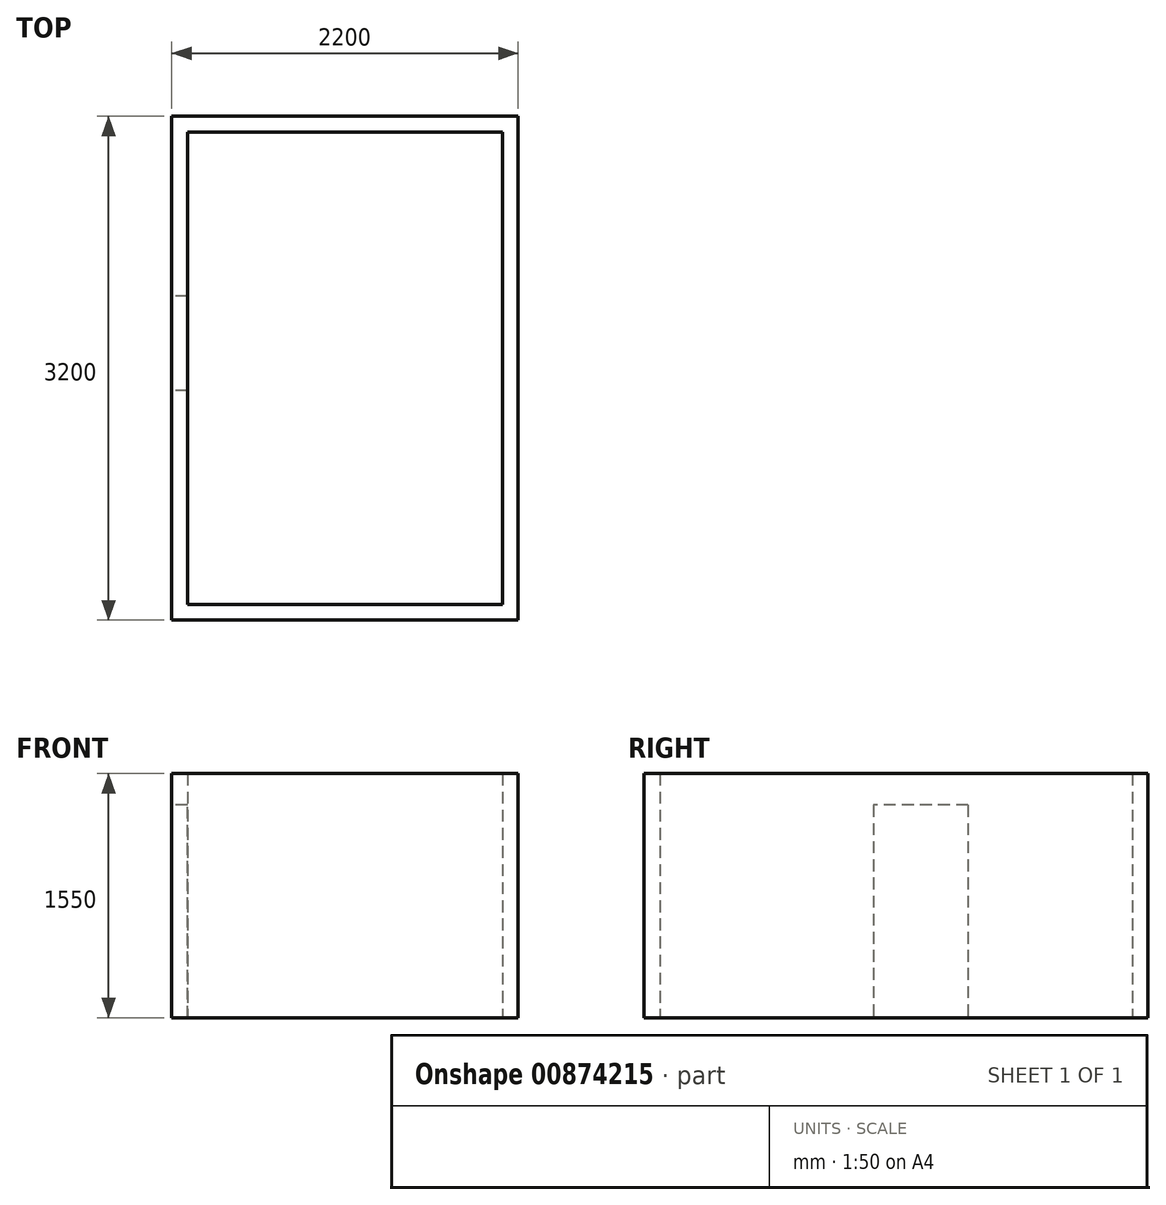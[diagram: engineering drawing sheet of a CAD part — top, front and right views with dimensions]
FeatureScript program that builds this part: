
annotation { "Feature Type Name" : "Feature", "Feature Type Description" : "" }
export const myFeature = defineFeature(function(context is Context, id is Id, definition is map)
    precondition{}
    {
        {
            var Q0;
            Q0=qCreatedBy(makeId("Top.planeOp"),FACE);
            var sketch = newSketch(context, id + "F0", { "sketchPlane" : qUnion([Q0])});
            skLineSegment(sketch, "E0", {"start": v(-780.9, 2929.22) * mm, "end": v(-780.9, -70.78) * mm});
            skLineSegment(sketch, "E1", {"start": v(-780.9, -70.78) * mm, "end": v(1219.1, -70.78) * mm});
            skLineSegment(sketch, "E2", {"start": v(1219.1, -70.78) * mm, "end": v(1219.1, 2929.22) * mm});
            skLineSegment(sketch, "E3", {"start": v(1219.1, 2929.22) * mm, "end": v(-780.9, 2929.22) * mm});
            skLineSegment(sketch, "E4", {"start": v(-780.9, 1429.22) * mm, "end": v(419.1, 1429.22) * mm});
            skLineSegment(sketch, "E5", {"start": v(419.1, 1429.22) * mm, "end": v(419.1, 2929.22) * mm});
            skArc(sketch, "E6", {"start": v(-480.9, 1429.22) * mm, "mid": v(-217.3, 2065.62) * mm, "end": v(419.1, 2329.22) * mm});
            skLineSegment(sketch, "E7.bottom", {"start": v(1219.1, 2929.22) * mm, "end": v(1319.1, 2929.22) * mm});
            skLineSegment(sketch, "E7.top", {"start": v(1219.1, -70.78) * mm, "end": v(1319.1, -70.78) * mm});
            skLineSegment(sketch, "E7.left", {"start": v(1219.1, 2929.22) * mm, "end": v(1219.1, -70.78) * mm});
            skLineSegment(sketch, "E7.right", {"start": v(1319.1, 2929.22) * mm, "end": v(1319.1, -70.78) * mm});
            skLineSegment(sketch, "E8.bottom", {"start": v(-780.9, 2929.22) * mm, "end": v(-880.9, 2929.22) * mm});
            skLineSegment(sketch, "E8.top", {"start": v(-780.9, -70.78) * mm, "end": v(-880.9, -70.78) * mm});
            skLineSegment(sketch, "E8.right", {"start": v(-880.9, 2929.22) * mm, "end": v(-880.9, -70.78) * mm});
            skLineSegment(sketch, "E9.bottom", {"start": v(-880.9, 2929.22) * mm, "end": v(1319.1, 2929.22) * mm});
            skLineSegment(sketch, "E9.top", {"start": v(-880.9, 3029.22) * mm, "end": v(1319.1, 3029.22) * mm});
            skLineSegment(sketch, "E9.left", {"start": v(-880.9, 2929.22) * mm, "end": v(-880.9, 3029.22) * mm});
            skLineSegment(sketch, "E9.right", {"start": v(1319.1, 2929.22) * mm, "end": v(1319.1, 3029.22) * mm});
            skLineSegment(sketch, "E10.bottom", {"start": v(-880.9, -70.78) * mm, "end": v(1319.1, -70.78) * mm});
            skLineSegment(sketch, "E10.top", {"start": v(-880.9, -170.78) * mm, "end": v(1319.1, -170.78) * mm});
            skLineSegment(sketch, "E10.left", {"start": v(-880.9, -70.78) * mm, "end": v(-880.9, -170.78) * mm});
            skLineSegment(sketch, "E10.right", {"start": v(1319.1, -70.78) * mm, "end": v(1319.1, -170.78) * mm});
            skLineSegment(sketch, "E11.bottom", {"start": v(-780.9, 1029.22) * mm, "end": v(519.1, 1029.22) * mm});
            skLineSegment(sketch, "E11.top", {"start": v(-780.9, 932.56) * mm, "end": v(519.1, 932.56) * mm});
            skLineSegment(sketch, "E11.left", {"start": v(-780.9, 932.56) * mm, "end": v(-780.9, 1029.22) * mm});
            skLineSegment(sketch, "E11.right", {"start": v(519.1, 932.56) * mm, "end": v(519.1, 1029.22) * mm});
            skLineSegment(sketch, "E12.bottom", {"start": v(519.1, 1029.22) * mm, "end": v(461.88, 1029.22) * mm});
            skLineSegment(sketch, "E12.top", {"start": v(519.1, -170.78) * mm, "end": v(461.88, -170.78) * mm});
            skLineSegment(sketch, "E12.left", {"start": v(519.1, 1029.22) * mm, "end": v(519.1, -170.78) * mm});
            skLineSegment(sketch, "E12.right", {"start": v(461.88, 1029.22) * mm, "end": v(461.88, -170.78) * mm});
            skArc(sketch, "E13", {"start": v(519.1, 375.57) * mm, "mid": v(164.6, 267.05) * mm, "end": v(11.88, -70.78) * mm});
            skLineSegment(sketch, "E14.bottom", {"start": v(1319.1, 1429.22) * mm, "end": v(850.33, 1429.22) * mm});
            skLineSegment(sketch, "E14.top", {"start": v(1319.1, 2929.22) * mm, "end": v(850.33, 2929.22) * mm});
            skLineSegment(sketch, "E14.left", {"start": v(1319.1, 1429.22) * mm, "end": v(1319.1, 2929.22) * mm});
            skLineSegment(sketch, "E14.right", {"start": v(850.33, 1429.22) * mm, "end": v(850.33, 2929.22) * mm});
            skArc(sketch, "E15", {"start": v(1319.1, 1785.5) * mm, "mid": v(1067.17, 1681.15) * mm, "end": v(962.82, 1429.22) * mm});
            skArc(sketch, "E16.trimOffspring", {"start": v(1219.1, 1087.27) * mm, "mid": v(1268.59, 1076.54) * mm, "end": v(1319.1, 1072.95) * mm});
            skSolve(sketch);
        }
        {
            var Q0;
            {var subQ0=sQuery(id+"F0.wireOp",EDGE,"E15");var subQ1=sQuery(id+"F0.wireOp",EDGE,"E2");var subQ2=makeQuery(id+"F0.imprint","INTERSECT",VERTEX,{"derivedFrom":[subQ1,subQ0]});Q0=makeQuery(id+"F0.imprint","IMPRINT",FACE,{"disambiguationData":[TD([[makeQuery(id+"F0.imprint","IMPRINT",EDGE,{"disambiguationData":[TD([[subQ2,1.0]])],"derivedFrom":subQ1}),-1.0]])]});}
            var Q1;
            {var subQ3=sQuery(id+"F0.wireOp",EDGE,"E16.trimOffspring");Q1=makeQuery(id+"F0.imprint","IMPRINT",FACE,{"disambiguationData":[TD([[makeQuery(id+"F0.imprint","IMPRINT",EDGE,{"derivedFrom":subQ3}),1.0]])]});}
            var Q2;
            {var subQ0=sQuery(id+"F0.wireOp",EDGE,"E7.top");Q2=makeQuery(id+"F0.imprint","IMPRINT",FACE,{"disambiguationData":[TD([[makeQuery(id+"F0.imprint","IMPRINT",EDGE,{"derivedFrom":subQ0}),1.0]])]});}
            var Q3;
            {var subQ0=sQuery(id+"F0.wireOp",EDGE,"E12.left");var subQ1=sQuery(id+"F0.wireOp",EDGE,"E1");var subQ2=makeQuery(id+"F0.imprint","INTERSECT",VERTEX,{"derivedFrom":[subQ1,subQ0]});Q3=makeQuery(id+"F0.imprint","IMPRINT",FACE,{"disambiguationData":[TD([[makeQuery(id+"F0.imprint","IMPRINT",EDGE,{"disambiguationData":[TD([[subQ2,1.0]])],"derivedFrom":subQ1}),-1.0]])]});}
            var Q4;
            {var subQ6=sQuery(id+"F0.wireOp",EDGE,"E7.top");Q4=makeQuery(id+"F0.imprint","IMPRINT",FACE,{"disambiguationData":[TD([[makeQuery(id+"F0.imprint","IMPRINT",EDGE,{"derivedFrom":subQ6}),-1.0]])]});}
            var Q5;
            {var subQ4=sQuery(id+"F0.wireOp",EDGE,"E8.top");Q5=makeQuery(id+"F0.imprint","IMPRINT",FACE,{"disambiguationData":[TD([[makeQuery(id+"F0.imprint","IMPRINT",EDGE,{"derivedFrom":subQ4}),1.0]])]});}
            var Q6;
            {var subQ0=sQuery(id+"F0.wireOp",EDGE,"E7.bottom");Q6=makeQuery(id+"F0.imprint","IMPRINT",FACE,{"disambiguationData":[TD([[makeQuery(id+"F0.imprint","IMPRINT",EDGE,{"derivedFrom":subQ0}),1.0]])]});}
            var Q7;
            {var subQ5=sQuery(id+"F0.wireOp",EDGE,"E8.bottom");Q7=makeQuery(id+"F0.imprint","IMPRINT",FACE,{"disambiguationData":[TD([[makeQuery(id+"F0.imprint","IMPRINT",EDGE,{"derivedFrom":subQ5}),1.0]])]});}
            var Q8;
            {var subQ3=sQuery(id+"F0.wireOp",EDGE,"E7.bottom");Q8=makeQuery(id+"F0.imprint","IMPRINT",FACE,{"disambiguationData":[TD([[makeQuery(id+"F0.imprint","IMPRINT",EDGE,{"derivedFrom":subQ3}),-1.0]])]});}
            extrude(context, id + "F1", {"entities" : qUnion([Q0, Q1, Q2, Q3, Q4, Q5, Q6, Q7, Q8]), "depth" : 1550 * mm, "offsetDistance" : 25 * mm});
        }
        {
            var Q0;
            Q0=makeQuery(id+"F1.opExtrude","SWEPT_FACE",FACE,{"disambiguationData":[OSD([sQuery(id+"F0.wireOp",EDGE,"E8.right"),sQuery(id+"F0.wireOp",EDGE,"E9.left"),sQuery(id+"F0.wireOp",EDGE,"E10.left")])]});
            var sketch = newSketch(context, id + "F2", { "sketchPlane" : qUnion([Q0])});
            skLineSegment(sketch, "E17.bottom", {"start": v(-1886.89, 1350) * mm, "end": v(-1286.89, 1350) * mm});
            skLineSegment(sketch, "E17.top", {"start": v(-1886.89, 0) * mm, "end": v(-1286.89, 0) * mm});
            skLineSegment(sketch, "E17.left", {"start": v(-1886.89, 1350) * mm, "end": v(-1886.89, 0) * mm});
            skLineSegment(sketch, "E17.right", {"start": v(-1286.89, 1350) * mm, "end": v(-1286.89, 0) * mm});
            skSolve(sketch);
        }
        {
            var Q0;
            Q0=makeQuery(id+"F2.imprint","IMPRINT",FACE,{"disambiguationData":[TD([[makeQuery(id+"F2.imprint","IMPRINT",EDGE,{"derivedFrom":sQuery(id+"F2.wireOp",EDGE,"E17.bottom")}),-1.0]])]});
            extrude(context, id + "F3", {"entities" : qUnion([Q0]), "operationType" : NewBodyOperationType.REMOVE, "oppositeDirection" : true, "depth" : 1090 * mm, "offsetDistance" : 25 * mm});
        }
    });
